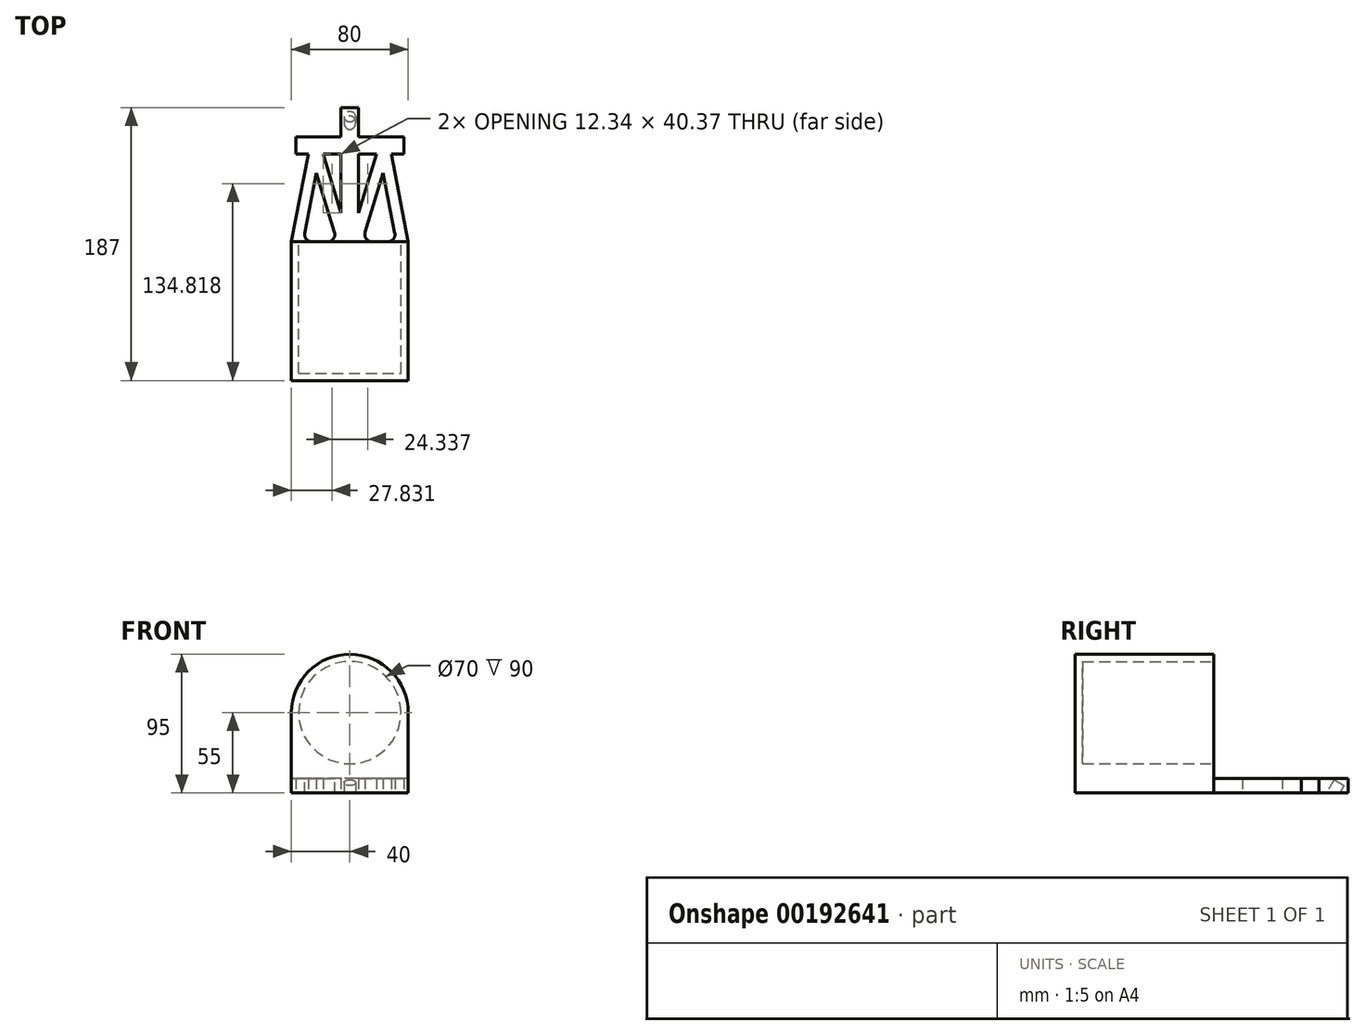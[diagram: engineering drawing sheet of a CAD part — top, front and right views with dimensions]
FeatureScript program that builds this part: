
annotation { "Feature Type Name" : "Feature", "Feature Type Description" : "" }
export const myFeature = defineFeature(function(context is Context, id is Id, definition is map)
    precondition{}
    {
        {
            var Q0;
            Q0=qCreatedBy(makeId("Top.planeOp"),FACE);
            var sketch = newSketch(context, id + "F0", { "sketchPlane" : qUnion([Q0])});
            skLineSegment(sketch, "E0", {"start": v(-6, 41.68) * mm, "end": v(-37, 41.68) * mm});
            skLineSegment(sketch, "E1", {"start": v(-37, 41.68) * mm, "end": v(-37, 29.68) * mm});
            skLineSegment(sketch, "E2", {"start": v(-37, 29.68) * mm, "end": v(-28.34, 29.68) * mm});
            skLineSegment(sketch, "E3", {"start": v(-6, 29.68) * mm, "end": v(-6, -10.69) * mm});
            skLineSegment(sketch, "E4", {"start": v(-8.52, -30.32) * mm, "end": v(-40, -30.32) * mm});
            skLineSegment(sketch, "E5", {"start": v(-40, -30.32) * mm, "end": v(-40, -125.32) * mm});
            skLineSegment(sketch, "E6", {"start": v(-40, -125.32) * mm, "end": v(0, -125.32) * mm});
            skLineSegment(sketch, "E7", {"start": v(-6, 41.68) * mm, "end": v(-6, 61.68) * mm});
            skLineSegment(sketch, "E8", {"start": v(-6, 61.68) * mm, "end": v(0, 61.68) * mm});
            skLineSegment(sketch, "E9.MirrorCS", {"start": v(8.52, -30.32) * mm, "end": v(40, -30.32) * mm});
            skLineSegment(sketch, "E10.MirrorCS", {"start": v(6, 29.68) * mm, "end": v(6, -10.69) * mm});
            skLineSegment(sketch, "E11.MirrorCS", {"start": v(37, 29.68) * mm, "end": v(28.34, 29.68) * mm});
            skLineSegment(sketch, "E12.MirrorCS", {"start": v(40, -125.32) * mm, "end": v(0, -125.32) * mm});
            skLineSegment(sketch, "E13.MirrorCS", {"start": v(6, 41.68) * mm, "end": v(37, 41.68) * mm});
            skLineSegment(sketch, "E14.MirrorCS", {"start": v(6, 41.68) * mm, "end": v(6, 61.68) * mm});
            skLineSegment(sketch, "E15.MirrorCS", {"start": v(40, -30.32) * mm, "end": v(40, -125.32) * mm});
            skLineSegment(sketch, "E16.MirrorCS", {"start": v(37, 41.68) * mm, "end": v(37, 29.68) * mm});
            skLineSegment(sketch, "E17.MirrorCS", {"start": v(6, 61.68) * mm, "end": v(0, 61.68) * mm});
            skLineSegment(sketch, "E18", {"start": v(-40, -30.32) * mm, "end": v(-28.34, 29.68) * mm});
            skLineSegment(sketch, "E19", {"start": v(-32, -30.32) * mm, "end": v(-22.87, 16.63) * mm});
            skLineSegment(sketch, "E20", {"start": v(-18.34, 29.68) * mm, "end": v(-6, -10.69) * mm});
            skLineSegment(sketch, "E21", {"start": v(-22.87, 16.63) * mm, "end": v(-8.52, -30.32) * mm});
            skPoint(sketch, "E22.orphan", {"position": v(-6, -30.32) * mm});
            skPoint(sketch, "E23.orphan", {"position": v(0, -30.32) * mm});
            skLineSegment(sketch, "E24.MirrorCS", {"start": v(18.34, 29.68) * mm, "end": v(6, -10.69) * mm});
            skLineSegment(sketch, "E25.MirrorCS", {"start": v(22.87, 16.63) * mm, "end": v(8.52, -30.32) * mm});
            skLineSegment(sketch, "E26.MirrorCS", {"start": v(40, -30.32) * mm, "end": v(28.34, 29.68) * mm});
            skLineSegment(sketch, "E27.MirrorCS", {"start": v(32, -30.32) * mm, "end": v(22.87, 16.63) * mm});
            skPoint(sketch, "E28.orphan", {"position": v(6, -30.32) * mm});
            skLineSegment(sketch, "E29.trimOffspring", {"start": v(18.34, 29.68) * mm, "end": v(6, 29.68) * mm});
            skLineSegment(sketch, "E30.trimOffspring", {"start": v(-18.34, 29.68) * mm, "end": v(-6, 29.68) * mm});
            skSolve(sketch);
        }
        {
            var Q0;
            Q0 = qSketchRegion(id + "F0", true);
            extrude(context, id + "F1", {"entities" : qUnion([Q0]), "depth" : 10 * mm});
        }
        {
            var Q0;
            Q0=makeQuery(id+"F1.opExtrude","CAP_FACE",FACE,{"disambiguationData":[OSD([sQuery(id+"F0.wireOp",EDGE,"E0"),sQuery(id+"F0.wireOp",EDGE,"E1"),sQuery(id+"F0.wireOp",EDGE,"E2"),sQuery(id+"F0.wireOp",EDGE,"E3"),sQuery(id+"F0.wireOp",EDGE,"E4"),sQuery(id+"F0.wireOp",EDGE,"E5"),sQuery(id+"F0.wireOp",EDGE,"E6"),sQuery(id+"F0.wireOp",EDGE,"E7"),sQuery(id+"F0.wireOp",EDGE,"E8"),sQuery(id+"F0.wireOp",EDGE,"E9.MirrorCS"),sQuery(id+"F0.wireOp",EDGE,"E10.MirrorCS"),sQuery(id+"F0.wireOp",EDGE,"E11.MirrorCS"),sQuery(id+"F0.wireOp",EDGE,"E12.MirrorCS"),sQuery(id+"F0.wireOp",EDGE,"E13.MirrorCS"),sQuery(id+"F0.wireOp",EDGE,"E14.MirrorCS"),sQuery(id+"F0.wireOp",EDGE,"E15.MirrorCS"),sQuery(id+"F0.wireOp",EDGE,"E16.MirrorCS"),sQuery(id+"F0.wireOp",EDGE,"E17.MirrorCS")])],"isStart":false});
            var sketch = newSketch(context, id + "F2", { "sketchPlane" : qUnion([Q0])});
            skLineSegment(sketch, "E31.0", {"start": v(-40, -30.32) * mm, "end": v(-40, -125.32) * mm});
            skPoint(sketch, "E32.0", {"position": v(-20.26, -30.32) * mm});
            skPoint(sketch, "E33.0", {"position": v(20.26, -30.32) * mm});
            skLineSegment(sketch, "E34.0", {"start": v(40, -30.32) * mm, "end": v(40, -125.32) * mm});
            skLineSegment(sketch, "E35.0", {"start": v(-40, -125.32) * mm, "end": v(40, -125.32) * mm});
            skLineSegment(sketch, "E36.0", {"start": v(-8.52, -30.32) * mm, "end": v(-40, -30.32) * mm});
            skLineSegment(sketch, "E37.0", {"start": v(8.52, -30.32) * mm, "end": v(40, -30.32) * mm});
            skLineSegment(sketch, "E38", {"start": v(-8.52, -30.32) * mm, "end": v(8.52, -30.32) * mm});
            skSolve(sketch);
        }
        {
            var Q0;
            Q0 = qSketchRegion(id + "F2", true);
            extrude(context, id + "F3", {"entities" : qUnion([Q0]), "operationType" : NewBodyOperationType.ADD, "depth" : 100 * mm});
        }
        {
            var Q0;
            Q0=makeQuery(id+"F3.boolean.opBoolean","MERGE",FACE,{"derivedFrom":[makeQuery(id+"F1.opExtrude","SWEPT_FACE",FACE,{"disambiguationData":[OSD([sQuery(id+"F0.wireOp",EDGE,"E4")])]}),makeQuery(id+"F1.opExtrude","SWEPT_FACE",FACE,{"disambiguationData":[OSD([sQuery(id+"F0.wireOp",EDGE,"E9.MirrorCS")])]}),makeQuery(id+"F3.opExtrude","SWEPT_FACE",FACE,{"disambiguationData":[OSD([sQuery(id+"F2.wireOp",EDGE,"ZSaGZZIM-98Oa-iZdK-xSvz-ztF0HBjywJkt"),sQuery(id+"F2.wireOp",EDGE,"E36.0"),sQuery(id+"F2.wireOp",EDGE,"E37.0")])]})]});
            var sketch = newSketch(context, id + "F4", { "sketchPlane" : qUnion([Q0])});
            skPoint(sketch, "E39.0", {"position": v(-40, 55) * mm});
            skPoint(sketch, "E40.0", {"position": v(0, 110) * mm});
            skCircle(sketch, "E41", {"center": v(0, 55) * mm, "radius": 35 * mm});
            skArc(sketch, "E42", {"start": v(40, 55) * mm, "mid": v(0, 95) * mm, "end": v(-40, 55) * mm});
            skLineSegment(sketch, "E43", {"start": v(40, 55) * mm, "end": v(40, 110) * mm});
            skLineSegment(sketch, "E44", {"start": v(40, 110) * mm, "end": v(-40, 110) * mm});
            skLineSegment(sketch, "E45", {"start": v(-40, 110) * mm, "end": v(-40, 55) * mm});
            skSolve(sketch);
        }
        {
            var Q0;
            Q0=makeQuery(id+"F4.imprint","IMPRINT",FACE,{"disambiguationData":[TD([[makeQuery(id+"F4.imprint","IMPRINT",EDGE,{"derivedFrom":sQuery(id+"F4.wireOp",EDGE,"E41")}),1.0]])]});
            extrude(context, id + "F5", {"entities" : qUnion([Q0]), "operationType" : NewBodyOperationType.REMOVE, "oppositeDirection" : true, "depth" : 90 * mm});
        }
        {
            var Q0;
            Q0=makeQuery(id+"F4.imprint","IMPRINT",FACE,{"disambiguationData":[TD([[makeQuery(id+"F4.imprint","IMPRINT",EDGE,{"derivedFrom":sQuery(id+"F4.wireOp",EDGE,"E42")}),-1.0]])]});
            extrude(context, id + "F6", {"entities" : qUnion([Q0]), "operationType" : NewBodyOperationType.REMOVE, "endBound" : BoundingType.THROUGH_ALL, "oppositeDirection" : true, "depth" : 25 * mm});
        }
        {
            var Q0;
            {var subQ1=sQuery(id+"F0.wireOp",EDGE,"E21");var subQ4=sQuery(id+"F2.wireOp",EDGE,"E38");var subQ5=sQuery(id+"F2.wireOp",EDGE,"E37.0");var subQ6=sQuery(id+"F2.wireOp",EDGE,"E36.0");Q0=makeQuery(id+"F3.boolean.opBoolean","SPLIT",EDGE,{"disambiguationData":[TD([makeQuery(id+"F1.opExtrude","SWEPT_FACE",FACE,{"disambiguationData":[OSD([subQ1])]})])],"derivedFrom":makeQuery(id+"F3.opExtrude","CAP_EDGE",EDGE,{"disambiguationData":[OSD([subQ6,subQ5,subQ4])],"isStart":true})});}
            var Q1;
            Q1=makeQuery(id+"F1.opExtrude","SWEPT_EDGE",EDGE,{"disambiguationData":[OSD([sQuery(id+"F0.wireOp",EDGE,"E4"),sQuery(id+"F0.wireOp",EDGE,"E21")])]});
            var Q2;
            Q2=makeQuery(id+"F1.opExtrude","SWEPT_EDGE",EDGE,{"disambiguationData":[OSD([sQuery(id+"F0.wireOp",EDGE,"E9.MirrorCS"),sQuery(id+"F0.wireOp",EDGE,"E25.MirrorCS")])]});
            var Q3;
            {var subQ0=sQuery(id+"F0.wireOp",EDGE,"E15.MirrorCS");var subQ5=sQuery(id+"F2.wireOp",EDGE,"E38");var subQ6=sQuery(id+"F2.wireOp",EDGE,"E37.0");var subQ7=sQuery(id+"F2.wireOp",EDGE,"E36.0");Q3=makeQuery(id+"F3.boolean.opBoolean","SPLIT",EDGE,{"disambiguationData":[TD([makeQuery(id+"F1.opExtrude","SWEPT_FACE",FACE,{"disambiguationData":[OSD([subQ0])]})])],"derivedFrom":makeQuery(id+"F3.opExtrude","CAP_EDGE",EDGE,{"disambiguationData":[OSD([subQ7,subQ6,subQ5])],"isStart":true})});}
            var Q4;
            Q4=makeQuery(id+"F1.opExtrude","SWEPT_EDGE",EDGE,{"disambiguationData":[OSD([sQuery(id+"F0.wireOp",EDGE,"E9.MirrorCS"),sQuery(id+"F0.wireOp",EDGE,"E27.MirrorCS")])]});
            var Q5;
            {var subQ1=sQuery(id+"F0.wireOp",EDGE,"E5");var subQ5=sQuery(id+"F2.wireOp",EDGE,"E38");var subQ6=sQuery(id+"F2.wireOp",EDGE,"E37.0");var subQ7=sQuery(id+"F2.wireOp",EDGE,"E36.0");Q5=makeQuery(id+"F3.boolean.opBoolean","SPLIT",EDGE,{"disambiguationData":[TD([makeQuery(id+"F1.opExtrude","SWEPT_FACE",FACE,{"disambiguationData":[OSD([subQ1])]})])],"derivedFrom":makeQuery(id+"F3.opExtrude","CAP_EDGE",EDGE,{"disambiguationData":[OSD([subQ7,subQ6,subQ5])],"isStart":true})});}
            var Q6;
            Q6=makeQuery(id+"F1.opExtrude","SWEPT_EDGE",EDGE,{"disambiguationData":[OSD([sQuery(id+"F0.wireOp",EDGE,"E4"),sQuery(id+"F0.wireOp",EDGE,"E19")])]});
            fillet(context, id + "F7", {"entities" : qUnion([Q0, Q1, Q2, Q3, Q4, Q5, Q6]), "radius" : 5 * mm, "tangentPropagation" : true, "allowEdgeOverflow" : false});
        }
        {
            var Q0;
            Q0=makeQuery(id+"F1.opExtrude","CAP_EDGE",EDGE,{"disambiguationData":[OSD([sQuery(id+"F0.wireOp",EDGE,"E13.MirrorCS")])],"isStart":true});
            var Q1;
            Q1=qCreatedBy(makeId("Top.planeOp"),FACE);
            cPlane(context, id + "F8", {"entities" : qUnion([Q0, Q1]), "cplaneType" : CPlaneType.LINE_ANGLE, "offset" : 25 * mm, "angle" : 150 * degree, "width" : 150 * mm, "height" : 150 * mm});
        }
        {
            var Q0;
            Q0=qCreatedBy(id+"F8.planeOp",FACE);
            cPlane(context, id + "F9", {"entities" : qUnion([Q0]), "cplaneType" : CPlaneType.OFFSET, "offset" : 5 * mm, "oppositeDirection" : true, "width" : 150 * mm, "height" : 150 * mm});
        }
        {
            var Q0;
            Q0=qCreatedBy(id+"F9.planeOp",FACE);
            var sketch = newSketch(context, id + "F10", { "sketchPlane" : qUnion([Q0])});
            skCircle(sketch, "E46", {"center": v(0, 44.42) * mm, "radius": 4 * mm});
            skSolve(sketch);
        }
        {
            var Q0;
            Q0 = qSketchRegion(id + "F10", true);
            extrude(context, id + "F11", {"entities" : qUnion([Q0]), "operationType" : NewBodyOperationType.REMOVE, "depth" : 18 * mm});
        }
    });
